# Revit family: LAMP_PUZZLE BLIND MODULE
name_source: partatom
category: Modelos genéricos
revit_build: Autodesk Revit 2015 (Build: 20140606_1530(x64)
units: mm (PartAtom-declared; Revit-internal decimal feet)

## types (2) — shared parameters
Accessory Type = Assembly
Elevación por defecto = 1219 mm
Fabricante = LAMP
Finish = Matte black
Installation instructions = http://www.lamp.es
Last update = 25/07/2018
Manufacturer URL = http://www.lamp.es
Manufacturer country = Spain
Manufacturer name = LAMP
Material tapa ciega = LAMP_Aluminio frame Puzzle BL
Product datasheet = http://www.lamp.es

## per-type parameters (varying)
| type | Descripción | Dimensions | Distancia | Modelo | Product code | Weight |
| MODULE A BLACK | PUZZLE ACC. IND BLIND MODULE BK. | 160 x 160 | 160 mm  [stored 0.524934 ft] | PUCOAB | PUCOAB | 0.15 kg |
| MODULE B BLACK | PUZZLE ACC. DB BLIND MODULE BK. | 320 x 160 | 320 mm  [stored 1.04987 ft] | PUCOBB | PUCOBB | 0.28 kg |

note: [stored X ft] marks values corroborated as IEEE doubles in the binary element streams (Revit-internal decimal feet)
